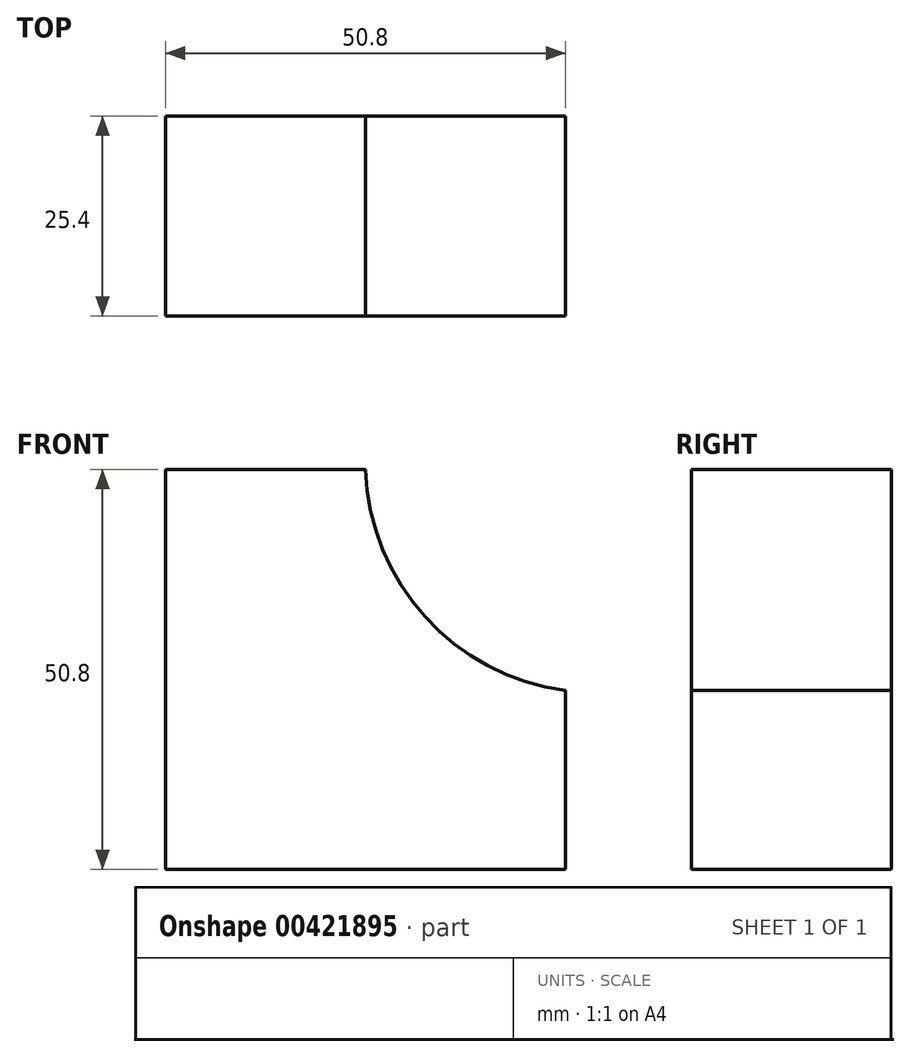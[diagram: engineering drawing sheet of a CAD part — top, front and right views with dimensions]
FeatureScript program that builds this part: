
annotation { "Feature Type Name" : "Feature", "Feature Type Description" : "" }
export const myFeature = defineFeature(function(context is Context, id is Id, definition is map)
    precondition{}
    {
        {
            var Q0;
            Q0=qCreatedBy(makeId("Front.planeOp"),FACE);
            var sketch = newSketch(context, id + "F0", { "sketchPlane" : qUnion([Q0])});
            skLineSegment(sketch, "E0", {"start": v(9.12, 0) * mm, "end": v(-41.68, 0) * mm});
            skLineSegment(sketch, "E1", {"start": v(-41.68, 0) * mm, "end": v(-41.68, 50.8) * mm});
            skLineSegment(sketch, "E2", {"start": v(-41.68, 50.8) * mm, "end": v(-16.28, 50.8) * mm});
            skLineSegment(sketch, "E3", {"start": v(9.12, 0) * mm, "end": v(9.12, 22.72) * mm});
            skArc(sketch, "E4", {"start": v(-16.28, 50.8) * mm, "mid": v(-8.72, 32.11) * mm, "end": v(9.12, 22.72) * mm});
            skSolve(sketch);
        }
        {
            var Q0;
            Q0=makeQuery(id+"F0.imprint","IMPRINT",FACE,{"disambiguationData":[TD([[makeQuery(id+"F0.imprint","IMPRINT",EDGE,{"derivedFrom":sQuery(id+"F0.wireOp",EDGE,"E0")}),-1.0]])]});
            extrude(context, id + "F1", {"entities" : qUnion([Q0]), "depth" : 25.4 * mm});
        }
    });
